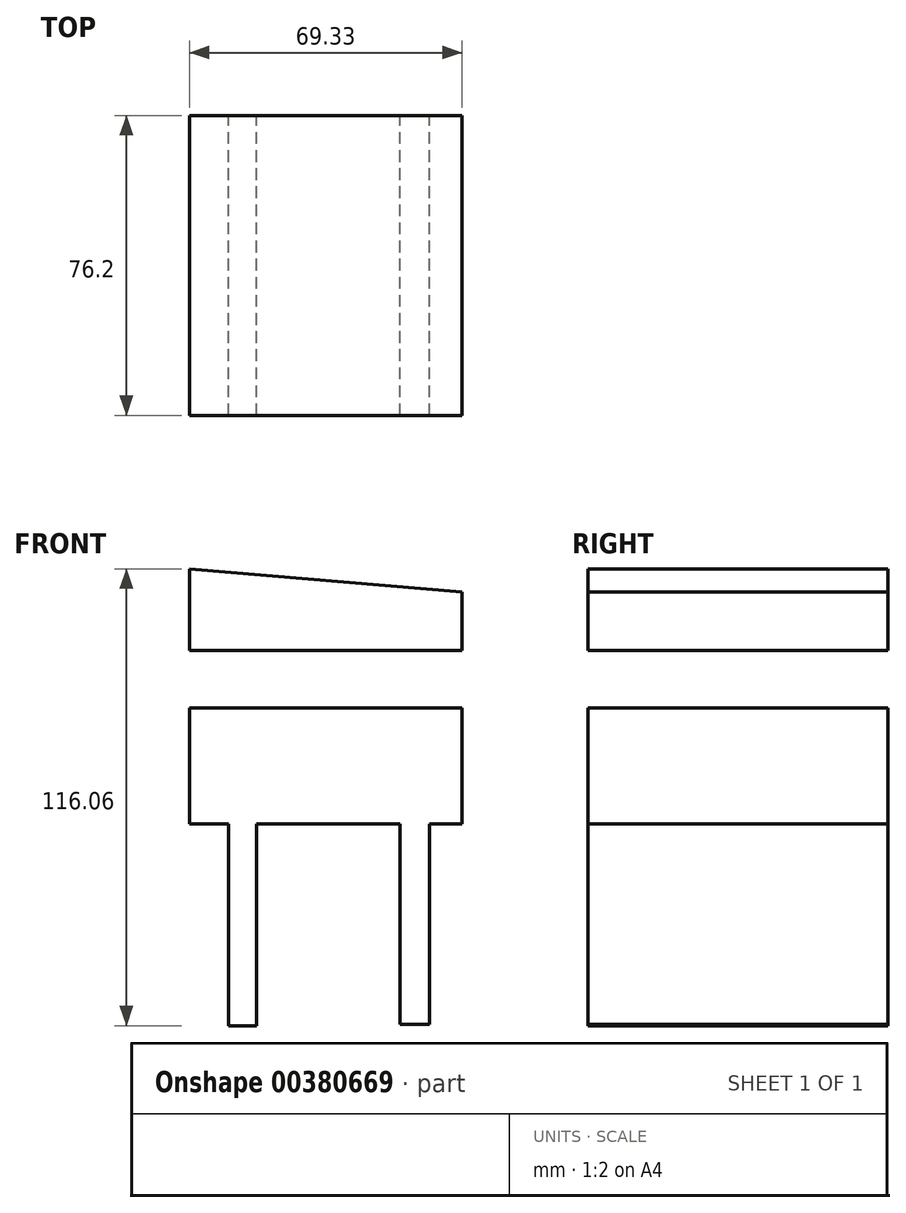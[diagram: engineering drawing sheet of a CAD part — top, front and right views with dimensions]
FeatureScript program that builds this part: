
annotation { "Feature Type Name" : "Feature", "Feature Type Description" : "" }
export const myFeature = defineFeature(function(context is Context, id is Id, definition is map)
    precondition{}
    {
        {
            var Q0;
            Q0=qCreatedBy(makeId("Front.planeOp"),FACE);
            var sketch = newSketch(context, id + "F0", { "sketchPlane" : qUnion([Q0])});
            skLineSegment(sketch, "E0", {"start": v(-65.62, 0) * mm, "end": v(-65.62, -51.22) * mm});
            skLineSegment(sketch, "E1", {"start": v(-65.62, -51.22) * mm, "end": v(-58.5, -51.22) * mm});
            skLineSegment(sketch, "E2", {"start": v(-58.5, -51.22) * mm, "end": v(-58.5, 0) * mm});
            skLineSegment(sketch, "E3", {"start": v(-58.5, 0) * mm, "end": v(-65.62, 0) * mm});
            skLineSegment(sketch, "E4", {"start": v(-21.98, 0) * mm, "end": v(-21.98, -50.92) * mm});
            skLineSegment(sketch, "E5", {"start": v(-21.98, -50.92) * mm, "end": v(-14.55, -50.92) * mm});
            skLineSegment(sketch, "E6", {"start": v(-14.55, -50.92) * mm, "end": v(-14.55, 0) * mm});
            skLineSegment(sketch, "E7", {"start": v(-14.55, 0) * mm, "end": v(-21.98, 0) * mm});
            skLineSegment(sketch, "E8", {"start": v(-75.52, 0) * mm, "end": v(-75.52, 64.84) * mm});
            skLineSegment(sketch, "E9", {"start": v(-75.52, 64.84) * mm, "end": v(-6.2, 58.96) * mm});
            skLineSegment(sketch, "E10", {"start": v(-6.2, 58.96) * mm, "end": v(-6.2, 0) * mm});
            skLineSegment(sketch, "E11", {"start": v(-6.2, 0) * mm, "end": v(-14.55, 0) * mm});
            skLineSegment(sketch, "E12", {"start": v(-75.52, 0) * mm, "end": v(-6.2, 0) * mm});
            skLineSegment(sketch, "E13", {"start": v(-75.52, 44.1) * mm, "end": v(-6.2, 44.1) * mm});
            skLineSegment(sketch, "E14", {"start": v(-6.2, 44.1) * mm, "end": v(-6.2, 29.48) * mm});
            skLineSegment(sketch, "E15", {"start": v(-6.2, 29.48) * mm, "end": v(-75.52, 29.48) * mm});
            skLineSegment(sketch, "E16", {"start": v(-75.52, 29.48) * mm, "end": v(-75.52, 44.1) * mm});
            skSolve(sketch);
        }
        {
            var Q0;
            {var subQ0=sQuery(id+"F0.wireOp",EDGE,"E9");Q0=makeQuery(id+"F0.imprint","IMPRINT",FACE,{"disambiguationData":[TD([[makeQuery(id+"F0.imprint","IMPRINT",EDGE,{"derivedFrom":subQ0}),-1.0]])]});}
            var Q1;
            {var subQ5=sQuery(id+"F0.wireOp",EDGE,"E15");Q1=makeQuery(id+"F0.imprint","IMPRINT",FACE,{"disambiguationData":[TD([[makeQuery(id+"F0.imprint","IMPRINT",EDGE,{"derivedFrom":subQ5}),1.0]])]});}
            extrude(context, id + "F1", {"entities" : qUnion([Q0, Q1]), "depth" : 76.2 * mm});
        }
        {
            var Q0;
            {var subQ0=sQuery(id+"F0.wireOp",EDGE,"E0");Q0=makeQuery(id+"F0.imprint","IMPRINT",FACE,{"disambiguationData":[TD([[makeQuery(id+"F0.imprint","IMPRINT",EDGE,{"derivedFrom":subQ0}),1.0]])]});}
            extrude(context, id + "F2", {"entities" : qUnion([Q0]), "operationType" : NewBodyOperationType.ADD, "depth" : 76.2 * mm});
        }
        {
            var Q0;
            {var subQ0=sQuery(id+"F0.wireOp",EDGE,"E4");Q0=makeQuery(id+"F0.imprint","IMPRINT",FACE,{"disambiguationData":[TD([[makeQuery(id+"F0.imprint","IMPRINT",EDGE,{"derivedFrom":subQ0}),1.0]])]});}
            extrude(context, id + "F3", {"entities" : qUnion([Q0]), "operationType" : NewBodyOperationType.ADD, "depth" : 76.2 * mm});
        }
    });
